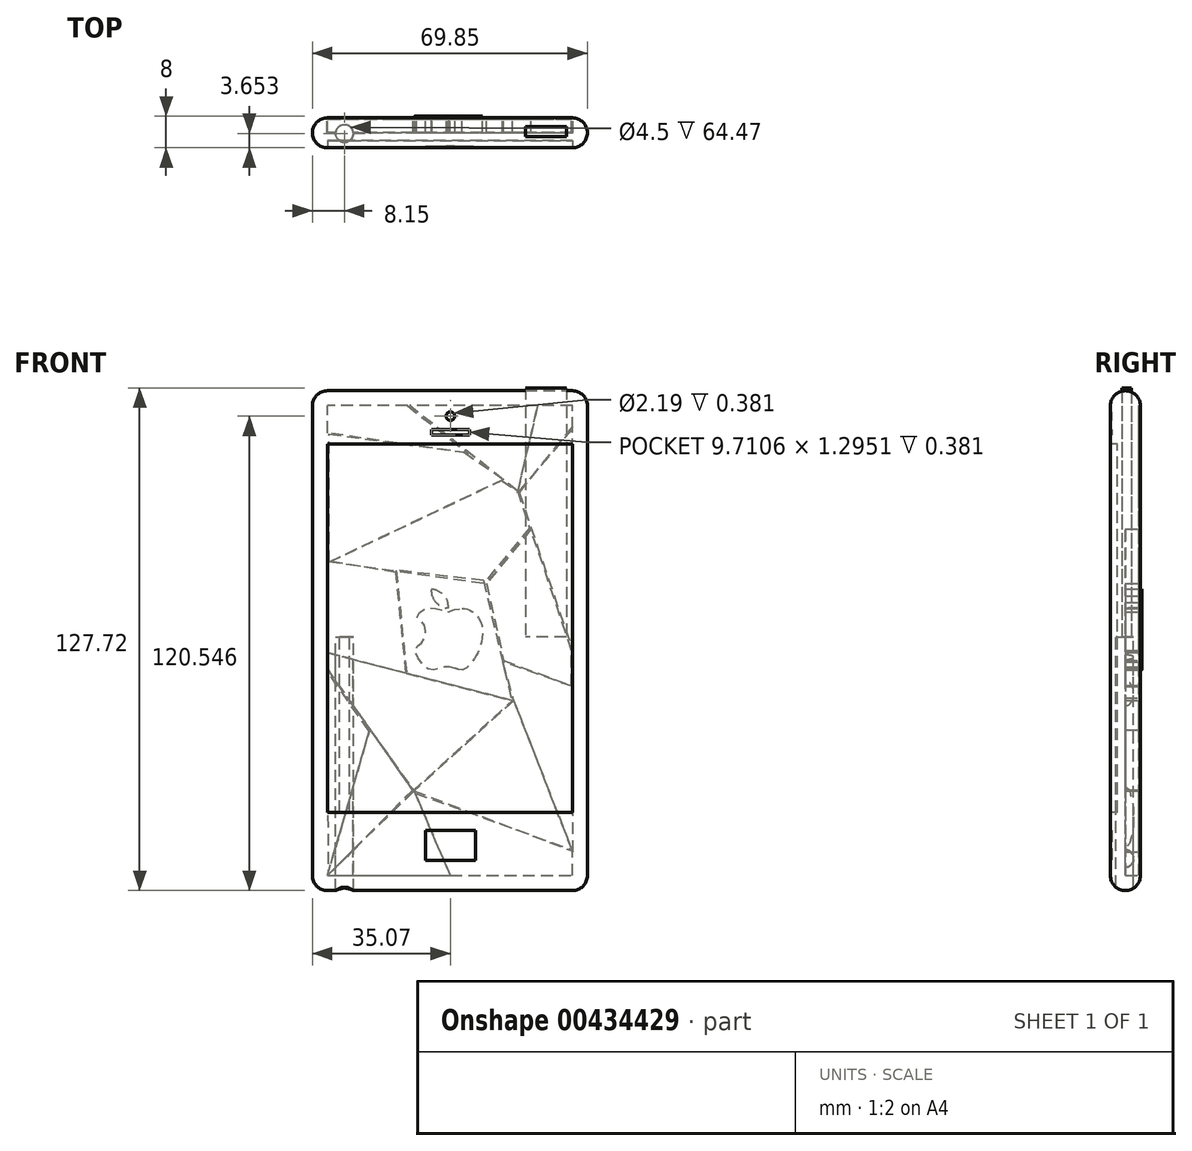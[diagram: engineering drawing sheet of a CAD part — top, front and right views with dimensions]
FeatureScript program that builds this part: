
annotation { "Feature Type Name" : "Feature", "Feature Type Description" : "" }
export const myFeature = defineFeature(function(context is Context, id is Id, definition is map)
    precondition{}
    {
        {
            var Q0;
            Q0=qCreatedBy(makeId("Front.planeOp"),FACE);
            var sketch = newSketch(context, id + "F0", { "sketchPlane" : qUnion([Q0])});
            skLineSegment(sketch, "E0", {"start": v(-35.07, -64.47) * mm, "end": v(34.78, -64.47) * mm});
            skLineSegment(sketch, "E1", {"start": v(34.78, -64.47) * mm, "end": v(34.78, 62.53) * mm});
            skLineSegment(sketch, "E2", {"start": v(-35.07, -64.47) * mm, "end": v(-35.07, 62.53) * mm});
            skLineSegment(sketch, "E3", {"start": v(34.78, 62.53) * mm, "end": v(-35.07, 62.53) * mm});
            skSolve(sketch);
        }
        {
            var Q0;
            Q0 = qSketchRegion(id + "F0", true);
            extrude(context, id + "F1", {"entities" : qUnion([Q0]), "depth" : 7.62 * mm});
        }
        {
            var Q0;
            Q0=makeQuery(id+"F1.opExtrude","CAP_EDGE",EDGE,{"disambiguationData":[OSD([sQuery(id+"F0.wireOp",EDGE,"E3")])],"isStart":false});
            var Q1;
            Q1=makeQuery(id+"F1.opExtrude","CAP_EDGE",EDGE,{"disambiguationData":[OSD([sQuery(id+"F0.wireOp",EDGE,"E3")])],"isStart":true});
            fillet(context, id + "F2", {"entities" : qUnion([Q0, Q1]), "radius" : 3.8 * mm, "tangentPropagation" : true, "allowEdgeOverflow" : false});
        }
        {
            var Q0;
            Q0=makeQuery(id+"F1.opExtrude","CAP_EDGE",EDGE,{"disambiguationData":[OSD([sQuery(id+"F0.wireOp",EDGE,"E0")])],"isStart":true});
            var Q1;
            Q1=makeQuery(id+"F1.opExtrude","CAP_EDGE",EDGE,{"disambiguationData":[OSD([sQuery(id+"F0.wireOp",EDGE,"E0")])],"isStart":false});
            fillet(context, id + "F3", {"entities" : qUnion([Q0, Q1]), "radius" : 3.8 * mm, "tangentPropagation" : true, "allowEdgeOverflow" : false});
        }
        {
            var Q0;
            Q0=makeQuery(id+"F1.opExtrude","CAP_EDGE",EDGE,{"disambiguationData":[OSD([sQuery(id+"F0.wireOp",EDGE,"E1")])],"isStart":false});
            var Q1;
            Q1=makeQuery(id+"F1.opExtrude","CAP_EDGE",EDGE,{"disambiguationData":[OSD([sQuery(id+"F0.wireOp",EDGE,"E1")])],"isStart":true});
            var Q2;
            Q2=makeQuery(id+"F2.opFillet","BLEND_EDGE",EDGE,{"blendedFrom":[makeQuery(id+"F1.opExtrude","CAP_EDGE",EDGE,{"disambiguationData":[OSD([sQuery(id+"F0.wireOp",EDGE,"E3")])],"isStart":false}),makeQuery(id+"F1.opExtrude","SWEPT_FACE",FACE,{"disambiguationData":[OSD([sQuery(id+"F0.wireOp",EDGE,"E1")])]})],"blendedInto":[makeQuery(id+"F1.opExtrude","SWEPT_FACE",FACE,{"disambiguationData":[OSD([sQuery(id+"F0.wireOp",EDGE,"E1")])]})]});
            var Q3;
            Q3=makeQuery(id+"F3.opFillet","BLEND_EDGE",EDGE,{"blendedFrom":[makeQuery(id+"F1.opExtrude","CAP_EDGE",EDGE,{"disambiguationData":[OSD([sQuery(id+"F0.wireOp",EDGE,"E0")])],"isStart":false}),makeQuery(id+"F1.opExtrude","SWEPT_FACE",FACE,{"disambiguationData":[OSD([sQuery(id+"F0.wireOp",EDGE,"E1")])]})],"blendedInto":[makeQuery(id+"F1.opExtrude","SWEPT_FACE",FACE,{"disambiguationData":[OSD([sQuery(id+"F0.wireOp",EDGE,"E1")])]})]});
            fillet(context, id + "F4", {"entities" : qUnion([Q0, Q1, Q2, Q3]), "radius" : 3.8 * mm, "tangentPropagation" : true, "allowEdgeOverflow" : false});
        }
        {
            var Q0;
            Q0=makeQuery(id+"F1.opExtrude","CAP_EDGE",EDGE,{"disambiguationData":[OSD([sQuery(id+"F0.wireOp",EDGE,"E2")])],"isStart":false});
            var Q1;
            Q1=makeQuery(id+"F1.opExtrude","CAP_EDGE",EDGE,{"disambiguationData":[OSD([sQuery(id+"F0.wireOp",EDGE,"E2")])],"isStart":true});
            var Q2;
            Q2=makeQuery(id+"F2.opFillet","BLEND_EDGE",EDGE,{"blendedFrom":[makeQuery(id+"F1.opExtrude","CAP_EDGE",EDGE,{"disambiguationData":[OSD([sQuery(id+"F0.wireOp",EDGE,"E3")])],"isStart":false}),makeQuery(id+"F1.opExtrude","SWEPT_FACE",FACE,{"disambiguationData":[OSD([sQuery(id+"F0.wireOp",EDGE,"E2")])]})],"blendedInto":[makeQuery(id+"F1.opExtrude","SWEPT_FACE",FACE,{"disambiguationData":[OSD([sQuery(id+"F0.wireOp",EDGE,"E2")])]})]});
            var Q3;
            Q3=makeQuery(id+"F3.opFillet","BLEND_EDGE",EDGE,{"blendedFrom":[makeQuery(id+"F1.opExtrude","CAP_EDGE",EDGE,{"disambiguationData":[OSD([sQuery(id+"F0.wireOp",EDGE,"E0")])],"isStart":false}),makeQuery(id+"F1.opExtrude","SWEPT_FACE",FACE,{"disambiguationData":[OSD([sQuery(id+"F0.wireOp",EDGE,"E2")])]})],"blendedInto":[makeQuery(id+"F1.opExtrude","SWEPT_FACE",FACE,{"disambiguationData":[OSD([sQuery(id+"F0.wireOp",EDGE,"E2")])]})]});
            fillet(context, id + "F5", {"entities" : qUnion([Q0, Q1, Q2, Q3]), "radius" : 3.8 * mm, "tangentPropagation" : true, "allowEdgeOverflow" : false});
        }
        {
            var Q0;
            Q0=makeQuery(id+"F1.opExtrude","CAP_FACE",FACE,{"disambiguationData":[OSD([sQuery(id+"F0.wireOp",EDGE,"E0"),sQuery(id+"F0.wireOp",EDGE,"E1"),sQuery(id+"F0.wireOp",EDGE,"E2"),sQuery(id+"F0.wireOp",EDGE,"E3")])],"isStart":false});
            var sketch = newSketch(context, id + "F6", { "sketchPlane" : qUnion([Q0])});
            skLineSegment(sketch, "E4", {"start": v(-31.26, -44.61) * mm, "end": v(30.97, -44.61) * mm});
            skLineSegment(sketch, "E5", {"start": v(30.97, -44.61) * mm, "end": v(30.97, 49.05) * mm});
            skLineSegment(sketch, "E6", {"start": v(30.97, 49.05) * mm, "end": v(-31.26, 49.05) * mm});
            skLineSegment(sketch, "E7", {"start": v(-31.26, 49.05) * mm, "end": v(-31.26, -44.61) * mm});
            skSolve(sketch);
        }
        {
            var Q0;
            Q0=makeQuery(id+"F6.imprint","IMPRINT",FACE,{"disambiguationData":[TD([[makeQuery(id+"F6.imprint","IMPRINT",EDGE,{"derivedFrom":sQuery(id+"F6.wireOp",EDGE,"E4")}),1.0]])]});
            extrude(context, id + "F7", {"entities" : qUnion([Q0]), "operationType" : NewBodyOperationType.REMOVE, "oppositeDirection" : true, "depth" : 1.78 * mm});
        }
        {
            var Q0;
            Q0=makeQuery(id+"F7.boolean.opBoolean","COPY",FACE,{"derivedFrom":makeQuery(id+"F7.opExtrude","CAP_FACE",FACE,{"disambiguationData":[OSD([sQuery(id+"F6.wireOp",EDGE,"E4"),sQuery(id+"F6.wireOp",EDGE,"E5"),sQuery(id+"F6.wireOp",EDGE,"E6"),sQuery(id+"F6.wireOp",EDGE,"E7")])],"isStart":false})});
            extrude(context, id + "F8", {"entities" : qUnion([Q0]), "depth" : 1.78 * mm});
        }
        {
            var Q0;
            {var subQ0=sQuery(id+"F0.wireOp",EDGE,"E2");var subQ1=sQuery(id+"F0.wireOp",EDGE,"E0");var subQ2=sQuery(id+"F0.wireOp",EDGE,"E1");Q0=makeQuery(id+"F7.boolean.opBoolean","SPLIT",FACE,{"disambiguationData":[TD([makeQuery(id+"F3.opFillet","BLEND_FACE",FACE,{"disambiguationData":[OSD([subQ1])]})])],"derivedFrom":makeQuery(id+"F1.opExtrude","CAP_FACE",FACE,{"disambiguationData":[OSD([subQ1,subQ2,subQ0,sQuery(id+"F0.wireOp",EDGE,"E3")])],"isStart":false})});}
            var sketch = newSketch(context, id + "F9", { "sketchPlane" : qUnion([Q0])});
            skLineSegment(sketch, "E8.bottom", {"start": v(-6.35, -49.12) * mm, "end": v(6.35, -49.12) * mm});
            skLineSegment(sketch, "E8.top", {"start": v(-6.35, -56.74) * mm, "end": v(6.35, -56.74) * mm});
            skLineSegment(sketch, "E8.left", {"start": v(-6.35, -49.12) * mm, "end": v(-6.35, -56.74) * mm});
            skLineSegment(sketch, "E8.right", {"start": v(6.35, -49.12) * mm, "end": v(6.35, -56.74) * mm});
            skPoint(sketch, "E8.middle", {"position": v(0, -52.93) * mm});
            skSolve(sketch);
        }
        {
            var Q0;
            {var subQ0=sQuery(id+"F0.wireOp",EDGE,"E3");var subQ1=sQuery(id+"F0.wireOp",EDGE,"E2");var subQ2=sQuery(id+"F0.wireOp",EDGE,"E1");Q0=makeQuery(id+"F7.boolean.opBoolean","SPLIT",FACE,{"disambiguationData":[TD([makeQuery(id+"F2.opFillet","BLEND_FACE",FACE,{"disambiguationData":[OSD([subQ0])]})])],"derivedFrom":makeQuery(id+"F1.opExtrude","CAP_FACE",FACE,{"disambiguationData":[OSD([sQuery(id+"F0.wireOp",EDGE,"E0"),subQ2,subQ1,subQ0])],"isStart":false})});}
            var sketch = newSketch(context, id + "F10", { "sketchPlane" : qUnion([Q0])});
            skCircle(sketch, "E9", {"center": v(0, 56.08) * mm, "radius": 1.1 * mm});
            skLineSegment(sketch, "E10.bottom", {"start": v(-4.86, 52.63) * mm, "end": v(4.86, 52.63) * mm});
            skLineSegment(sketch, "E10.top", {"start": v(-4.86, 51.33) * mm, "end": v(4.86, 51.33) * mm});
            skLineSegment(sketch, "E10.left", {"start": v(-4.86, 52.63) * mm, "end": v(-4.86, 51.33) * mm});
            skLineSegment(sketch, "E10.right", {"start": v(4.86, 52.63) * mm, "end": v(4.86, 51.33) * mm});
            skPoint(sketch, "E10.middle", {"position": v(0, 51.98) * mm});
            skSolve(sketch);
        }
        {
            var Q0;
            Q0 = qSketchRegion(id + "F10", true);
            extrude(context, id + "F11", {"entities" : qUnion([Q0]), "operationType" : NewBodyOperationType.REMOVE, "oppositeDirection" : true, "depth" : 0.38 * mm});
        }
        {
            var Q0;
            Q0 = qSketchRegion(id + "F9", true);
            extrude(context, id + "F12", {"entities" : qUnion([Q0]), "oppositeDirection" : true, "depth" : 0.38 * mm});
        }
        {
            var Q0;
            Q0=makeQuery(id+"F1.opExtrude","CAP_FACE",FACE,{"disambiguationData":[OSD([sQuery(id+"F0.wireOp",EDGE,"E0"),sQuery(id+"F0.wireOp",EDGE,"E1"),sQuery(id+"F0.wireOp",EDGE,"E2"),sQuery(id+"F0.wireOp",EDGE,"E3")])],"isStart":true});
            var sketch = newSketch(context, id + "F13", { "sketchPlane" : qUnion([Q0])});
            skLineSegment(sketch, "E11", {"start": v(-30.97, 52.82) * mm, "end": v(-17.07, 36.6) * mm});
            skLineSegment(sketch, "E12", {"start": v(-17.07, 36.6) * mm, "end": v(-22.15, 58.72) * mm});
            skLineSegment(sketch, "E13", {"start": v(-22.15, 58.72) * mm, "end": v(-30.97, 58.72) * mm});
            skLineSegment(sketch, "E14", {"start": v(-30.97, 58.72) * mm, "end": v(-30.97, 52.82) * mm});
            skSolve(sketch);
        }
        {
            var Q0;
            Q0 = qSketchRegion(id + "F13", true);
            extrude(context, id + "F14", {"entities" : qUnion([Q0]), "oppositeDirection" : true, "depth" : 0.38 * mm});
        }
        {
            var Q0;
            Q0=makeQuery(id+"F1.opExtrude","CAP_FACE",FACE,{"disambiguationData":[OSD([sQuery(id+"F0.wireOp",EDGE,"E0"),sQuery(id+"F0.wireOp",EDGE,"E1"),sQuery(id+"F0.wireOp",EDGE,"E2"),sQuery(id+"F0.wireOp",EDGE,"E3")])],"isStart":true});
            var sketch = newSketch(context, id + "F15", { "sketchPlane" : qUnion([Q0])});
            skLineSegment(sketch, "E15", {"start": v(-17.04, 37.04) * mm, "end": v(10.34, 58.72) * mm});
            skLineSegment(sketch, "E16", {"start": v(10.34, 58.72) * mm, "end": v(-22.17, 58.72) * mm});
            skLineSegment(sketch, "E17", {"start": v(-22.17, 58.72) * mm, "end": v(-17.04, 37.04) * mm});
            skSolve(sketch);
        }
        {
            var Q0;
            Q0 = qSketchRegion(id + "F15", true);
            extrude(context, id + "F16", {"entities" : qUnion([Q0]), "oppositeDirection" : true, "depth" : 0.38 * mm});
        }
        {
            var Q0;
            Q0=makeQuery(id+"F1.opExtrude","CAP_FACE",FACE,{"disambiguationData":[OSD([sQuery(id+"F0.wireOp",EDGE,"E0"),sQuery(id+"F0.wireOp",EDGE,"E1"),sQuery(id+"F0.wireOp",EDGE,"E2"),sQuery(id+"F0.wireOp",EDGE,"E3")])],"isStart":true});
            var sketch = newSketch(context, id + "F17", { "sketchPlane" : qUnion([Q0])});
            skLineSegment(sketch, "E18", {"start": v(-17.44, 36.76) * mm, "end": v(-30.97, -3.24) * mm});
            skLineSegment(sketch, "E19", {"start": v(-30.97, -3.24) * mm, "end": v(-30.97, 53.45) * mm});
            skLineSegment(sketch, "E20", {"start": v(-30.97, 53.45) * mm, "end": v(-17.44, 36.76) * mm});
            skSolve(sketch);
        }
        {
            var Q0;
            Q0 = qSketchRegion(id + "F17", true);
            extrude(context, id + "F18", {"entities" : qUnion([Q0]), "oppositeDirection" : true, "depth" : 0.38 * mm});
        }
        {
            var Q0;
            Q0=makeQuery(id+"F1.opExtrude","CAP_FACE",FACE,{"disambiguationData":[OSD([sQuery(id+"F0.wireOp",EDGE,"E0"),sQuery(id+"F0.wireOp",EDGE,"E1"),sQuery(id+"F0.wireOp",EDGE,"E2"),sQuery(id+"F0.wireOp",EDGE,"E3")])],"isStart":true});
            var sketch = newSketch(context, id + "F19", { "sketchPlane" : qUnion([Q0])});
            skLineSegment(sketch, "E21", {"start": v(-4.6, 46.62) * mm, "end": v(31.26, 51.8) * mm});
            skLineSegment(sketch, "E22", {"start": v(31.26, 51.8) * mm, "end": v(31.26, 58.72) * mm});
            skLineSegment(sketch, "E23", {"start": v(31.26, 58.72) * mm, "end": v(10.94, 58.72) * mm});
            skLineSegment(sketch, "E24", {"start": v(10.94, 58.72) * mm, "end": v(-4.6, 46.62) * mm});
            skSolve(sketch);
        }
        {
            var Q0;
            Q0 = qSketchRegion(id + "F19", true);
            extrude(context, id + "F20", {"entities" : qUnion([Q0]), "oppositeDirection" : true, "depth" : 0.38 * mm});
        }
        {
            var Q0;
            Q0=makeQuery(id+"F1.opExtrude","CAP_FACE",FACE,{"disambiguationData":[OSD([sQuery(id+"F0.wireOp",EDGE,"E0"),sQuery(id+"F0.wireOp",EDGE,"E1"),sQuery(id+"F0.wireOp",EDGE,"E2"),sQuery(id+"F0.wireOp",EDGE,"E3")])],"isStart":true});
            var sketch = newSketch(context, id + "F21", { "sketchPlane" : qUnion([Q0])});
            skPoint(sketch, "E25.47.internal.snap0", {"position": v(0.51, 12.7) * mm});
            skFitSpline(sketch, "E25", {"points": [v(-2.55, -8.74) * mm, v(-2.06, -8.29) * mm, v(-1.23, -8) * mm, v(-0.66, -7.92) * mm, v(0, -7.73) * mm, v(0.66, -7.63) * mm, v(1, -7.63) * mm, v(1.6, -7.66) * mm, v(2.25, -7.9) * mm, v(2.85, -8.1) * mm, v(3.38, -8.22) * mm, v(4.15, -8.46) * mm, v(4.6, -8.46) * mm, v(5.4, -8.36) * mm, v(6.34, -7.63) * mm, v(7.1, -6.83) * mm, v(7.66, -6.07) * mm, v(8.46, -4.97) * mm, v(8.99, -3.64) * mm, v(9.12, -3.01) * mm, v(8.66, -2.62) * mm, v(8.26, -2.22) * mm, v(7.83, -1.92) * mm, v(7.4, -1.52) * mm, v(6.97, -0.96) * mm, v(6.63, -0.53) * mm, v(6.4, 0.5) * mm, v(6.3, 1.46) * mm, v(6.37, 2.16) * mm, v(6.57, 2.82) * mm, v(6.8, 3.32) * mm, v(7.16, 3.79) * mm, v(7.46, 4.35) * mm, v(8.03, 4.75) * mm, v(8.6, 5.11) * mm, v(8.31, 5.7) * mm, v(7.78, 6.24) * mm, v(7.39, 6.57) * mm, v(6.92, 6.83) * mm, v(6.22, 7.07) * mm, v(5.56, 7.3) * mm, v(4.53, 7.36) * mm, v(4.07, 7.33) * mm, v(3.2, 7.13) * mm, v(2.4, 6.93) * mm, v(1.75, 6.63) * mm, v(0.95, 6.37) * mm, v(0.51, 6.3) * mm, v(-0.61, 6.73) * mm, v(-1.8, 7.17) * mm, v(-2.93, 7.2) * mm], "startDerivative": vector(22.32, 25.58) * mm, "endDerivative": vector(-45.77, -1.64) * mm});
            skFitSpline(sketch, "E26", {"points": [v(-2.93, 7.2) * mm, v(-3.48, 7.2) * mm, v(-3.74, 7.2) * mm, v(-4.11, 7.06) * mm, v(-4.57, 6.92) * mm, v(-5.06, 6.7) * mm, v(-5.51, 6.46) * mm, v(-5.95, 6.17) * mm, v(-6.4, 5.77) * mm, v(-7.03, 5) * mm, v(-7.37, 4.45) * mm, v(-7.88, 3.27) * mm, v(-8.16, 2.14) * mm, v(-8.16, 1.5) * mm, v(-8.1, 0) * mm, v(-7.88, -1.25) * mm, v(-7.61, -2.37) * mm, v(-7.44, -2.84) * mm, v(-7.08, -3.77) * mm, v(-6.8, -4.38) * mm, v(-6.49, -5.01) * mm, v(-5.8, -6) * mm, v(-5.23, -6.75) * mm, v(-4.28, -7.78) * mm, v(-3.2, -8.37) * mm, v(-2.06, -8.29) * mm, v(-1.23, -8) * mm], "startDerivative": vector(-19.4, -0.45) * mm, "endDerivative": vector(19.6, 8.14) * mm});
            skFitSpline(sketch, "E27", {"points": [v(0.52, 7.34) * mm, v(0.54, 8.02) * mm, v(0.64, 8.67) * mm], "startDerivative": vector(0, 1.36) * mm, "endDerivative": vector(0.24, 1.3) * mm});
            skLineSegment(sketch, "E28", {"start": v(0.52, 7.34) * mm, "end": v(1.05, 7.34) * mm});
            skFitSpline(sketch, "E29", {"points": [v(4.83, 12.21) * mm, v(4.86, 11.93) * mm, v(4.87, 11.58) * mm, v(4.85, 11.22) * mm, v(4.78, 10.8) * mm, v(4.67, 10.4) * mm], "startDerivative": vector(0.17, -1.54) * mm, "endDerivative": vector(-0.56, -1.86) * mm});
            skFitSpline(sketch, "E30", {"points": [v(4.67, 10.4) * mm, v(4.47, 10) * mm, v(4.27, 9.6) * mm, v(3.95, 9.16) * mm, v(3.73, 8.86) * mm, v(3.63, 8.75) * mm, v(3.3, 8.42) * mm, v(2.94, 8.1) * mm, v(2.75, 7.95) * mm, v(2.46, 7.81) * mm, v(2.06, 7.58) * mm, v(1.4, 7.36) * mm, v(1.05, 7.34) * mm], "startDerivative": vector(-2.3, -4.6) * mm, "endDerivative": vector(-4.06, 0.08) * mm});
            skFitSpline(sketch, "E31", {"points": [v(4.83, 12.21) * mm, v(4.26, 12.1) * mm, v(3.79, 11.99) * mm, v(3.38, 11.8) * mm, v(2.96, 11.59) * mm, v(2.57, 11.35) * mm, v(2.1, 11) * mm, v(1.78, 10.65) * mm, v(1.46, 10.29) * mm, v(1.22, 9.91) * mm, v(0.98, 9.5) * mm, v(0.79, 9.05) * mm, v(0.64, 8.67) * mm], "startDerivative": vector(-6.36, -1.26) * mm, "endDerivative": vector(-1.95, -4.76) * mm});
            skSolve(sketch);
        }
        {
            var Q0;
            Q0=makeQuery(id+"F21.imprint","IMPRINT",FACE,{"disambiguationData":[TD([[makeQuery(id+"F21.imprint","IMPRINT",EDGE,{"derivedFrom":sQuery(id+"F21.wireOp",EDGE,"E27")}),1.0]])]});
            var sketch = newSketch(context, id + "F22", { "sketchPlane" : qUnion([Q0])});
            skLineSegment(sketch, "E32", {"start": v(-13.53, 40) * mm, "end": v(30.8, 19) * mm});
            skLineSegment(sketch, "E33", {"start": v(30.8, 19) * mm, "end": v(30.8, 51.52) * mm});
            skLineSegment(sketch, "E34", {"start": v(30.8, 51.52) * mm, "end": v(-3.45, 46.91) * mm});
            skLineSegment(sketch, "E35", {"start": v(-3.45, 46.91) * mm, "end": v(-13.53, 40) * mm});
            skSolve(sketch);
        }
        {
            var Q0;
            Q0 = qSketchRegion(id + "F22", true);
            extrude(context, id + "F23", {"entities" : qUnion([Q0]), "oppositeDirection" : true, "depth" : 0.38 * mm});
        }
        {
            var Q0;
            Q0=makeQuery(id+"F21.imprint","IMPRINT",FACE,{"disambiguationData":[TD([[makeQuery(id+"F21.imprint","IMPRINT",EDGE,{"derivedFrom":sQuery(id+"F21.wireOp",EDGE,"E27")}),1.0]])]});
            var sketch = newSketch(context, id + "F24", { "sketchPlane" : qUnion([Q0])});
            skLineSegment(sketch, "E36", {"start": v(-20.15, 27.63) * mm, "end": v(-8.35, 13.53) * mm});
            skLineSegment(sketch, "E37", {"start": v(-8.35, 13.53) * mm, "end": v(30.8, 19) * mm});
            skLineSegment(sketch, "E38", {"start": v(30.8, 19) * mm, "end": v(-12.95, 39.72) * mm});
            skLineSegment(sketch, "E39", {"start": v(-12.95, 39.72) * mm, "end": v(-16.98, 37.13) * mm});
            skLineSegment(sketch, "E40", {"start": v(-16.98, 37.13) * mm, "end": v(-20.15, 27.63) * mm});
            skSolve(sketch);
        }
        {
            var Q0;
            Q0 = qSketchRegion(id + "F24", true);
            extrude(context, id + "F25", {"entities" : qUnion([Q0]), "oppositeDirection" : true, "depth" : 0.38 * mm});
        }
        {
            var Q0;
            Q0=makeQuery(id+"F21.imprint","IMPRINT",FACE,{"disambiguationData":[TD([[makeQuery(id+"F21.imprint","IMPRINT",EDGE,{"derivedFrom":sQuery(id+"F21.wireOp",EDGE,"E27")}),1.0]])]});
            var sketch = newSketch(context, id + "F26", { "sketchPlane" : qUnion([Q0])});
            skLineSegment(sketch, "E41", {"start": v(-9.2, 13.53) * mm, "end": v(-13.53, -6.04) * mm});
            skLineSegment(sketch, "E42", {"start": v(-13.53, -6.04) * mm, "end": v(-30.8, -12.38) * mm});
            skLineSegment(sketch, "E43", {"start": v(-30.8, -12.38) * mm, "end": v(-30.8, -3.45) * mm});
            skLineSegment(sketch, "E44", {"start": v(-30.8, -3.45) * mm, "end": v(-20.43, 27.34) * mm});
            skLineSegment(sketch, "E45", {"start": v(-20.43, 27.34) * mm, "end": v(-9.2, 13.53) * mm});
            skSolve(sketch);
        }
        {
            var Q0;
            Q0 = qSketchRegion(id + "F26", true);
            extrude(context, id + "F27", {"entities" : qUnion([Q0]), "oppositeDirection" : true, "depth" : 3.8 * mm});
        }
        {
            var Q0;
            Q0=makeQuery(id+"F21.imprint","IMPRINT",FACE,{"disambiguationData":[TD([[makeQuery(id+"F21.imprint","IMPRINT",EDGE,{"derivedFrom":sQuery(id+"F21.wireOp",EDGE,"E27")}),1.0]])]});
            var sketch = newSketch(context, id + "F28", { "sketchPlane" : qUnion([Q0])});
            skLineSegment(sketch, "E46", {"start": v(11.22, -9.2) * mm, "end": v(13.81, 16.4) * mm});
            skLineSegment(sketch, "E47", {"start": v(13.81, 16.4) * mm, "end": v(31.08, 19.28) * mm});
            skLineSegment(sketch, "E48", {"start": v(31.08, 19.28) * mm, "end": v(31.08, -4.03) * mm});
            skLineSegment(sketch, "E49", {"start": v(31.08, -4.03) * mm, "end": v(11.22, -9.2) * mm});
            skSolve(sketch);
        }
        {
            var Q0;
            Q0 = qSketchRegion(id + "F28", true);
            extrude(context, id + "F29", {"entities" : qUnion([Q0]), "oppositeDirection" : true, "depth" : 0.38 * mm});
        }
        {
            var Q0;
            Q0=makeQuery(id+"F21.imprint","IMPRINT",FACE,{"disambiguationData":[TD([[makeQuery(id+"F21.imprint","IMPRINT",EDGE,{"derivedFrom":sQuery(id+"F21.wireOp",EDGE,"E27")}),1.0]])]});
            var sketch = newSketch(context, id + "F30", { "sketchPlane" : qUnion([Q0])});
            skLineSegment(sketch, "E50", {"start": v(20.72, -23.89) * mm, "end": v(31.08, -59.86) * mm});
            skLineSegment(sketch, "E51", {"start": v(20.72, -23.89) * mm, "end": v(31.37, -8.63) * mm});
            skLineSegment(sketch, "E52", {"start": v(31.37, -8.63) * mm, "end": v(31.08, -59.86) * mm});
            skSolve(sketch);
        }
        {
            var Q0;
            Q0 = qSketchRegion(id + "F30", true);
            extrude(context, id + "F31", {"entities" : qUnion([Q0]), "oppositeDirection" : true, "depth" : 0.38 * mm});
        }
        {
            var Q0;
            Q0=makeQuery(id+"F21.imprint","IMPRINT",FACE,{"disambiguationData":[TD([[makeQuery(id+"F21.imprint","IMPRINT",EDGE,{"derivedFrom":sQuery(id+"F21.wireOp",EDGE,"E27")}),1.0]])]});
            var sketch = newSketch(context, id + "F32", { "sketchPlane" : qUnion([Q0])});
            skLineSegment(sketch, "E53", {"start": v(31.37, -4.03) * mm, "end": v(-15.83, -16.12) * mm});
            skLineSegment(sketch, "E54", {"start": v(31.37, -4.03) * mm, "end": v(31.37, -8.06) * mm});
            skLineSegment(sketch, "E55", {"start": v(31.37, -8.06) * mm, "end": v(9.5, -39.14) * mm});
            skLineSegment(sketch, "E56", {"start": v(9.5, -39.14) * mm, "end": v(-15.83, -16.12) * mm});
            skSolve(sketch);
        }
        {
            var Q0;
            Q0 = qSketchRegion(id + "F32", true);
            extrude(context, id + "F33", {"entities" : qUnion([Q0]), "oppositeDirection" : true, "depth" : 3.8 * mm});
        }
        {
            var Q0;
            Q0=makeQuery(id+"F21.imprint","IMPRINT",FACE,{"disambiguationData":[TD([[makeQuery(id+"F21.imprint","IMPRINT",EDGE,{"derivedFrom":sQuery(id+"F21.wireOp",EDGE,"E27")}),1.0]])]});
            var sketch = newSketch(context, id + "F34", { "sketchPlane" : qUnion([Q0])});
            skLineSegment(sketch, "E57", {"start": v(-13.24, -6.33) * mm, "end": v(-15.83, -15.54) * mm});
            skLineSegment(sketch, "E58", {"start": v(-15.83, -15.54) * mm, "end": v(-31.08, -54.68) * mm});
            skLineSegment(sketch, "E59", {"start": v(-31.08, -54.68) * mm, "end": v(-31.08, -12.66) * mm});
            skLineSegment(sketch, "E60", {"start": v(-31.08, -12.66) * mm, "end": v(-13.24, -6.33) * mm});
            skSolve(sketch);
        }
        {
            var Q0;
            Q0 = qSketchRegion(id + "F34", true);
            extrude(context, id + "F35", {"entities" : qUnion([Q0]), "oppositeDirection" : true, "depth" : 3.8 * mm});
        }
        {
            var Q0;
            Q0 = qSketchRegion(id + "F21", true);
            extrude(context, id + "F36", {"entities" : qUnion([Q0]), "operationType" : NewBodyOperationType.REMOVE, "oppositeDirection" : true, "depth" : 3.8 * mm});
        }
        {
            var Q0;
            Q0 = qSketchRegion(id + "F21", true);
            extrude(context, id + "F37", {"entities" : qUnion([Q0]), "operationType" : NewBodyOperationType.ADD, "depth" : 0.38 * mm});
        }
        {
            var Q0;
            Q0=makeQuery(id+"F1.opExtrude","CAP_FACE",FACE,{"disambiguationData":[OSD([sQuery(id+"F0.wireOp",EDGE,"E0"),sQuery(id+"F0.wireOp",EDGE,"E1"),sQuery(id+"F0.wireOp",EDGE,"E2"),sQuery(id+"F0.wireOp",EDGE,"E3")])],"isStart":true});
            var sketch = newSketch(context, id + "F38", { "sketchPlane" : qUnion([Q0])});
            skLineSegment(sketch, "E61", {"start": v(9.2, -39.14) * mm, "end": v(-30.97, -54.4) * mm});
            skLineSegment(sketch, "E62", {"start": v(-30.97, -54.4) * mm, "end": v(-16.12, -16.12) * mm});
            skLineSegment(sketch, "E63", {"start": v(-16.12, -16.12) * mm, "end": v(9.2, -39.14) * mm});
            skSolve(sketch);
        }
        {
            var Q0;
            Q0 = qSketchRegion(id + "F38", true);
            extrude(context, id + "F39", {"entities" : qUnion([Q0]), "oppositeDirection" : true, "depth" : 0.38 * mm});
        }
        {
            var Q0;
            Q0=makeQuery(id+"F1.opExtrude","CAP_FACE",FACE,{"disambiguationData":[OSD([sQuery(id+"F0.wireOp",EDGE,"E0"),sQuery(id+"F0.wireOp",EDGE,"E1"),sQuery(id+"F0.wireOp",EDGE,"E2"),sQuery(id+"F0.wireOp",EDGE,"E3")])],"isStart":true});
            var sketch = newSketch(context, id + "F40", { "sketchPlane" : qUnion([Q0])});
            skLineSegment(sketch, "E64", {"start": v(9.5, -38.85) * mm, "end": v(31.26, -60.66) * mm});
            skLineSegment(sketch, "E65", {"start": v(31.26, -60.66) * mm, "end": v(20.43, -23.6) * mm});
            skLineSegment(sketch, "E66", {"start": v(20.43, -23.6) * mm, "end": v(9.5, -38.85) * mm});
            skSolve(sketch);
        }
        {
            var Q0;
            Q0 = qSketchRegion(id + "F40", true);
            extrude(context, id + "F41", {"entities" : qUnion([Q0]), "oppositeDirection" : true, "depth" : 3.8 * mm});
        }
        {
            var Q0;
            Q0=makeQuery(id+"F1.opExtrude","CAP_FACE",FACE,{"disambiguationData":[OSD([sQuery(id+"F0.wireOp",EDGE,"E0"),sQuery(id+"F0.wireOp",EDGE,"E1"),sQuery(id+"F0.wireOp",EDGE,"E2"),sQuery(id+"F0.wireOp",EDGE,"E3")])],"isStart":true});
            var sketch = newSketch(context, id + "F42", { "sketchPlane" : qUnion([Q0])});
            skLineSegment(sketch, "E67", {"start": v(9.2, -39.14) * mm, "end": v(0.14, -60.66) * mm});
            skLineSegment(sketch, "E68", {"start": v(0.14, -60.66) * mm, "end": v(31.26, -60.66) * mm});
            skLineSegment(sketch, "E69", {"start": v(31.26, -60.66) * mm, "end": v(9.2, -39.14) * mm});
            skSolve(sketch);
        }
        {
            var Q0;
            Q0 = qSketchRegion(id + "F42", true);
            extrude(context, id + "F43", {"entities" : qUnion([Q0]), "oppositeDirection" : true, "depth" : 3.8 * mm});
        }
        {
            var Q0;
            Q0=makeQuery(id+"F1.opExtrude","CAP_FACE",FACE,{"disambiguationData":[OSD([sQuery(id+"F0.wireOp",EDGE,"E0"),sQuery(id+"F0.wireOp",EDGE,"E1"),sQuery(id+"F0.wireOp",EDGE,"E2"),sQuery(id+"F0.wireOp",EDGE,"E3")])],"isStart":true});
            var sketch = newSketch(context, id + "F44", { "sketchPlane" : qUnion([Q0])});
            skLineSegment(sketch, "E70", {"start": v(8.92, -39.72) * mm, "end": v(-30.97, -54.1) * mm});
            skLineSegment(sketch, "E71", {"start": v(-30.97, -54.1) * mm, "end": v(-30.97, -60.66) * mm});
            skLineSegment(sketch, "E72", {"start": v(-30.97, -60.66) * mm, "end": v(0, -60.66) * mm});
            skLineSegment(sketch, "E73", {"start": v(0, -60.66) * mm, "end": v(8.92, -39.72) * mm});
            skSolve(sketch);
        }
        {
            var Q0;
            Q0 = qSketchRegion(id + "F44", true);
            extrude(context, id + "F45", {"entities" : qUnion([Q0]), "oppositeDirection" : true, "depth" : 0.38 * mm});
        }
        {
            var Q0;
            Q0=makeQuery(id+"F1.opExtrude","CAP_FACE",FACE,{"disambiguationData":[OSD([sQuery(id+"F0.wireOp",EDGE,"E0"),sQuery(id+"F0.wireOp",EDGE,"E1"),sQuery(id+"F0.wireOp",EDGE,"E2"),sQuery(id+"F0.wireOp",EDGE,"E3")])],"isStart":true});
            var sketch = newSketch(context, id + "F46", { "sketchPlane" : qUnion([Q0])});
            skLineSegment(sketch, "E74", {"start": v(-8.4, 14.3) * mm, "end": v(-15.59, -16.2) * mm});
            skLineSegment(sketch, "E75", {"start": v(-8.4, 14.3) * mm, "end": v(13.77, 16.9) * mm});
            skLineSegment(sketch, "E76", {"start": v(13.77, 16.9) * mm, "end": v(11.18, -9.3) * mm});
            skLineSegment(sketch, "E77", {"start": v(11.18, -9.3) * mm, "end": v(-15.59, -16.2) * mm});
            skSolve(sketch);
        }
        {
            var Q0;
            Q0 = qSketchRegion(id + "F46", true);
            extrude(context, id + "F47", {"entities" : qUnion([Q0]), "oppositeDirection" : true, "depth" : 0.38 * mm});
        }
        {
            var Q0;
            Q0=qCreatedBy(makeId("Top.planeOp"),FACE);
            var sketch = newSketch(context, id + "F48", { "sketchPlane" : qUnion([Q0])});
            skLineSegment(sketch, "E78.bottom", {"start": v(29.43, -2.3) * mm, "end": v(19.02, -2.3) * mm});
            skLineSegment(sketch, "E78.top", {"start": v(29.43, -4.71) * mm, "end": v(19.02, -4.71) * mm});
            skLineSegment(sketch, "E78.left", {"start": v(29.43, -2.3) * mm, "end": v(29.43, -4.71) * mm});
            skLineSegment(sketch, "E78.right", {"start": v(19.02, -2.3) * mm, "end": v(19.02, -4.71) * mm});
            skPoint(sketch, "E78.middle", {"position": v(24.23, -3.5) * mm});
            skSolve(sketch);
        }
        {
            var Q0;
            Q0 = qSketchRegion(id + "F48", true);
            extrude(context, id + "F49", {"entities" : qUnion([Q0]), "depth" : 63.25 * mm});
        }
        {
            var Q0;
            Q0=qCreatedBy(makeId("Top.planeOp"),FACE);
            var sketch = newSketch(context, id + "F50", { "sketchPlane" : qUnion([Q0])});
            skCircle(sketch, "E79", {"center": v(-26.92, -3.97) * mm, "radius": 2.25 * mm});
            skSolve(sketch);
        }
        {
            var Q0;
            Q0 = qSketchRegion(id + "F50", true);
            extrude(context, id + "F51", {"entities" : qUnion([Q0]), "operationType" : NewBodyOperationType.REMOVE, "oppositeDirection" : true, "depth" : 85.34 * mm});
        }
    });
